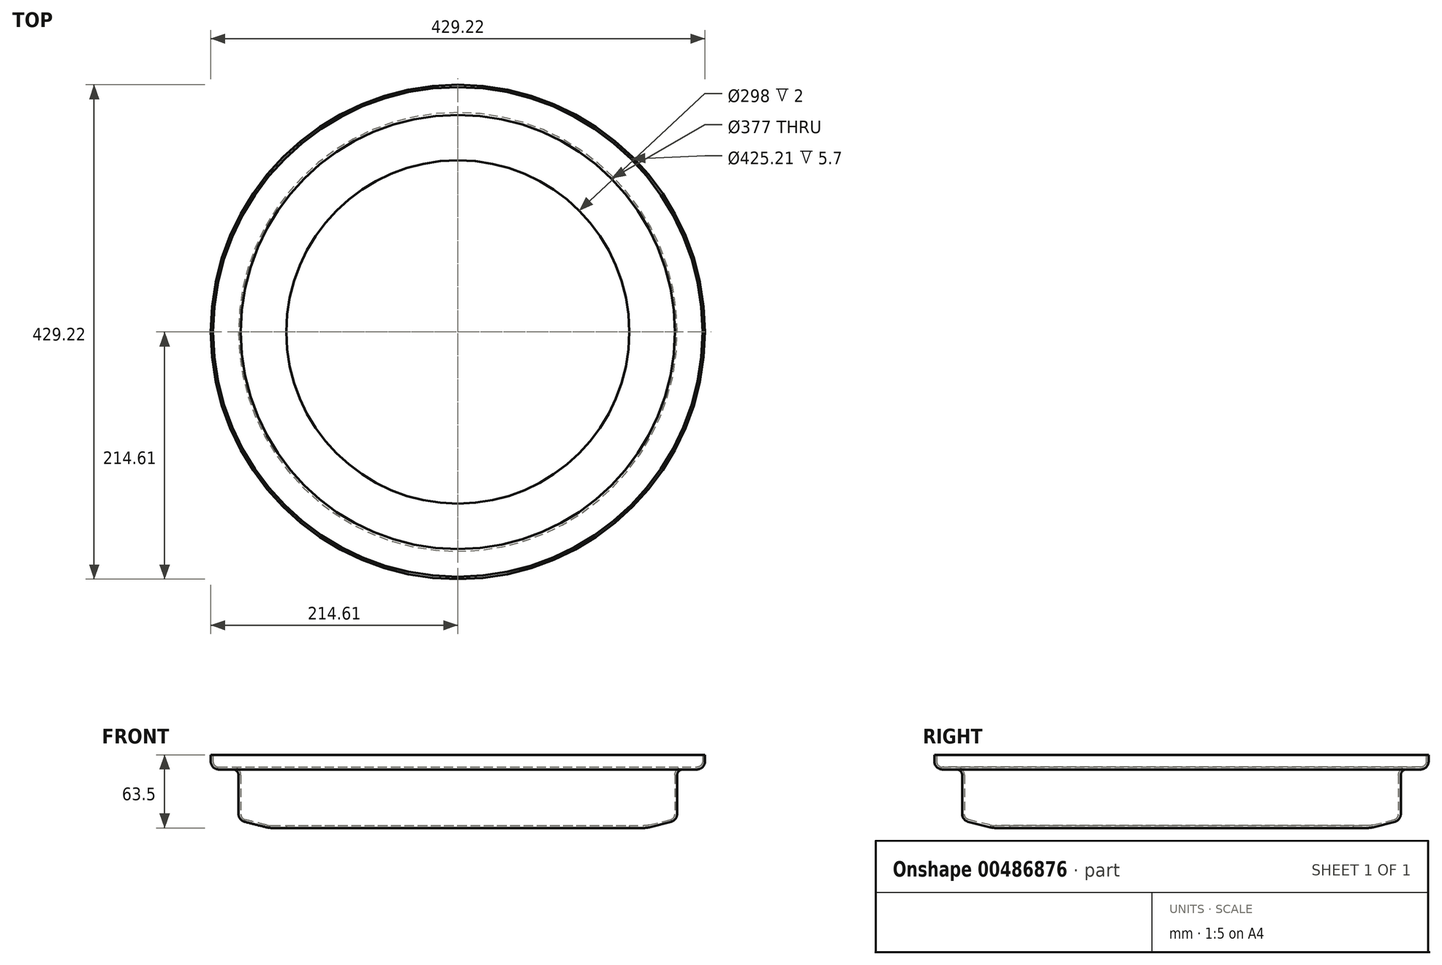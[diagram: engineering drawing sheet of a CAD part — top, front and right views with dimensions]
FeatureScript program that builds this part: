
annotation { "Feature Type Name" : "Feature", "Feature Type Description" : "" }
export const myFeature = defineFeature(function(context is Context, id is Id, definition is map)
    precondition{}
    {
        {
            var Q0;
            Q0=qCreatedBy(makeId("Front.planeOp"),FACE);
            var sketch = newSketch(context, id + "F0", { "sketchPlane" : qUnion([Q0])});
            skLineSegment(sketch, "E0", {"start": v(-149, 0) * mm, "end": v(-161.53, 0) * mm});
            skLineSegment(sketch, "E1", {"start": v(-149, 0) * mm, "end": v(-149, 2) * mm});
            skLineSegment(sketch, "E2", {"start": v(-149, 2) * mm, "end": v(-161.53, 2) * mm});
            skLineSegment(sketch, "E3", {"start": v(-166.4, 2.6) * mm, "end": v(-184.72, 7.2) * mm});
            skLineSegment(sketch, "E4", {"start": v(-188.5, 12.06) * mm, "end": v(-188.5, 45.8) * mm});
            skLineSegment(sketch, "E5", {"start": v(-195.5, 52.8) * mm, "end": v(-207.6, 52.8) * mm});
            skLineSegment(sketch, "E6", {"start": v(-212.6, 57.8) * mm, "end": v(-212.6, 63.5) * mm});
            skLineSegment(sketch, "E7", {"start": v(-212.6, 63.5) * mm, "end": v(-214.6, 63.5) * mm});
            skLineSegment(sketch, "E8", {"start": v(-214.6, 63.5) * mm, "end": v(-214.6, 57.8) * mm});
            skLineSegment(sketch, "E9", {"start": v(-207.6, 50.8) * mm, "end": v(-195.5, 50.8) * mm});
            skLineSegment(sketch, "E10", {"start": v(-190.5, 45.8) * mm, "end": v(-190.5, 12.12) * mm});
            skLineSegment(sketch, "E11", {"start": v(-185.2, 5.33) * mm, "end": v(-166.4, 0.6) * mm});
            skLineSegment(sketch, "E12", {"start": v(0, 0) * mm, "end": v(0, 45.18) * mm, "construction": true});
            skPoint(sketch, "E13.visualSharp", {"position": v(-164, 2) * mm});
            skArc(sketch, "E13.filletArc", {"start": v(-166.4, 2.6) * mm, "mid": v(-163.98, 2.15) * mm, "end": v(-161.53, 2) * mm});
            skPoint(sketch, "E14.visualSharp", {"position": v(-164, 0) * mm});
            skArc(sketch, "E14.filletArc", {"start": v(-166.4, 0.6) * mm, "mid": v(-163.98, 0.15) * mm, "end": v(-161.53, 0) * mm});
            skPoint(sketch, "E15.visualSharp", {"position": v(-188.5, 8.16) * mm});
            skArc(sketch, "E15.filletArc", {"start": v(-188.5, 12.06) * mm, "mid": v(-187.44, 8.98) * mm, "end": v(-184.72, 7.2) * mm});
            skPoint(sketch, "E16.visualSharp", {"position": v(-190.5, 6.66) * mm});
            skArc(sketch, "E16.filletArc", {"start": v(-190.5, 12.12) * mm, "mid": v(-189.02, 7.81) * mm, "end": v(-185.2, 5.33) * mm});
            skPoint(sketch, "E17.visualSharp", {"position": v(-188.5, 52.8) * mm});
            skArc(sketch, "E17.filletArc", {"start": v(-188.5, 45.8) * mm, "mid": v(-190.55, 50.75) * mm, "end": v(-195.5, 52.8) * mm});
            skPoint(sketch, "E18.visualSharp", {"position": v(-190.5, 50.8) * mm});
            skArc(sketch, "E18.filletArc", {"start": v(-190.5, 45.8) * mm, "mid": v(-191.96, 49.34) * mm, "end": v(-195.5, 50.8) * mm});
            skPoint(sketch, "E19.visualSharp", {"position": v(-212.6, 52.8) * mm});
            skArc(sketch, "E19.filletArc", {"start": v(-212.6, 57.8) * mm, "mid": v(-211.14, 54.26) * mm, "end": v(-207.6, 52.8) * mm});
            skPoint(sketch, "E20.visualSharp", {"position": v(-214.6, 50.8) * mm});
            skArc(sketch, "E20.filletArc", {"start": v(-214.6, 57.8) * mm, "mid": v(-212.56, 52.85) * mm, "end": v(-207.6, 50.8) * mm});
            skSolve(sketch);
        }
        {
            var Q0;
            Q0=makeQuery(id+"F0.imprint","IMPRINT",FACE,{"disambiguationData":[TD([[makeQuery(id+"F0.imprint","IMPRINT",EDGE,{"derivedFrom":sQuery(id+"F0.wireOp",EDGE,"E0")}),-1.0]])]});
            var Q1;
            Q1=sQuery(id+"F0.wireOp",EDGE,"E12");
            revolve(context, id + "F1", {"entities" : qUnion([Q0]), "axis" : qUnion([Q1]), "revolveType" : RevolveType.FULL});
        }
    });
